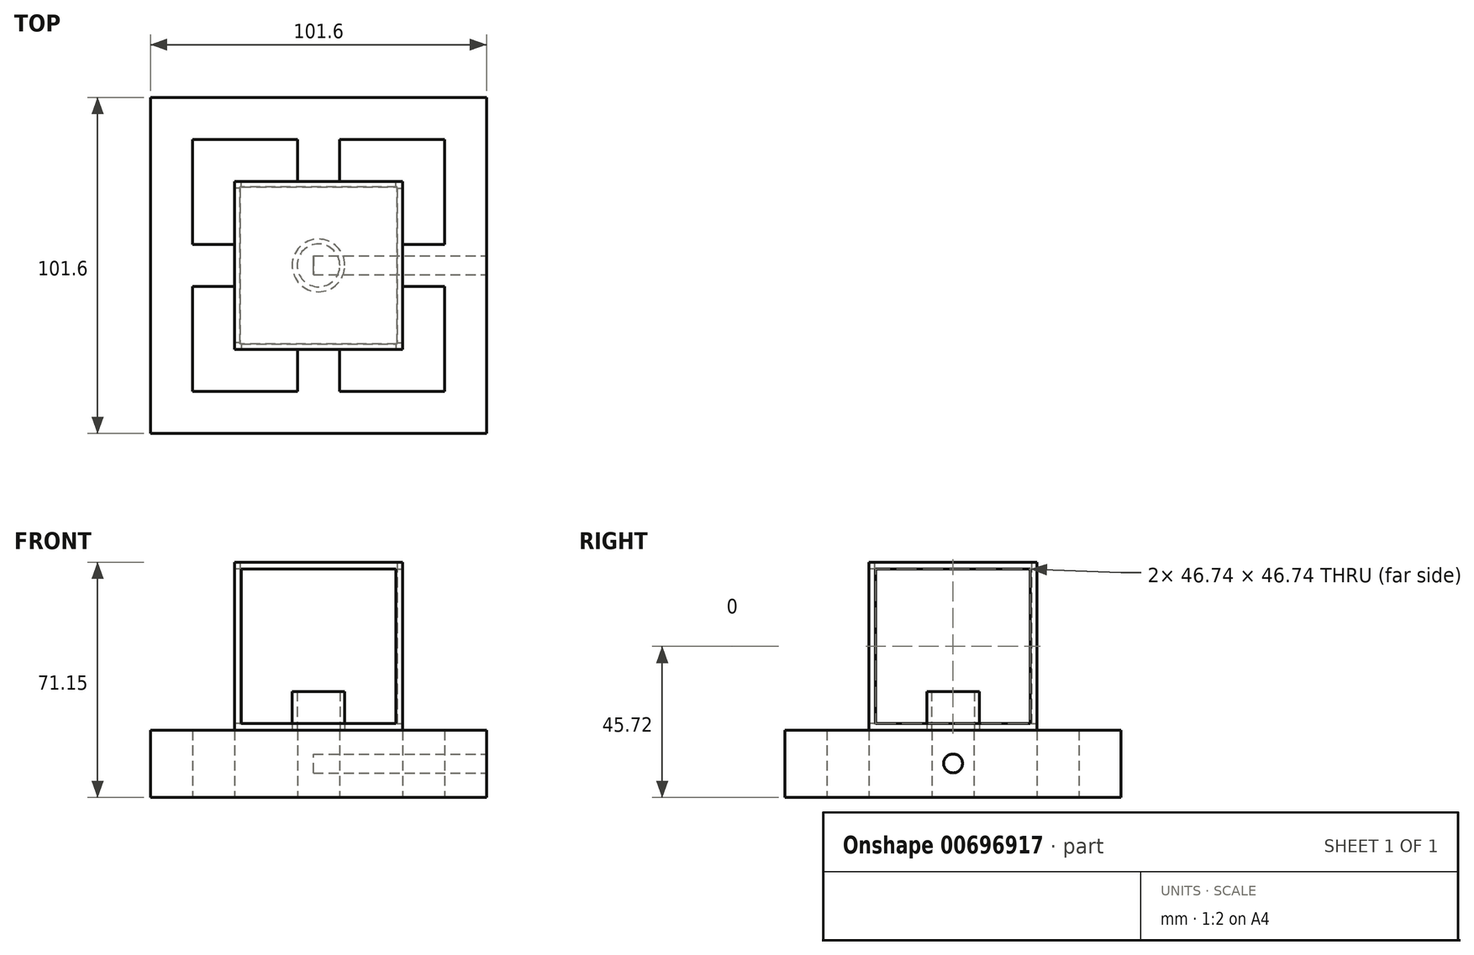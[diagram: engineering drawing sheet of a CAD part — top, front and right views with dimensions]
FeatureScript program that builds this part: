
annotation { "Feature Type Name" : "Feature", "Feature Type Description" : "" }
export const myFeature = defineFeature(function(context is Context, id is Id, definition is map)
    precondition{}
    {
        {
            var Q0;
            Q0=qCreatedBy(makeId("Top.planeOp"),FACE);
            var sketch = newSketch(context, id + "F0", { "sketchPlane" : qUnion([Q0])});
            skLineSegment(sketch, "E0.bottom", {"start": v(50.8, -50.8) * mm, "end": v(-50.8, -50.8) * mm});
            skLineSegment(sketch, "E0.top", {"start": v(50.8, 50.8) * mm, "end": v(-50.8, 50.8) * mm});
            skLineSegment(sketch, "E0.left", {"start": v(50.8, -50.8) * mm, "end": v(50.8, 50.8) * mm});
            skLineSegment(sketch, "E0.right", {"start": v(-50.8, -50.8) * mm, "end": v(-50.8, 50.8) * mm});
            skPoint(sketch, "E0.middle", {"position": v(0, 0) * mm});
            skLineSegment(sketch, "E1.bottom", {"start": v(38.1, -38.1) * mm, "end": v(6.35, -38.1) * mm});
            skLineSegment(sketch, "E1.top", {"start": v(38.1, 38.1) * mm, "end": v(6.35, 38.1) * mm});
            skLineSegment(sketch, "E1.left", {"start": v(38.1, -38.1) * mm, "end": v(38.1, -6.35) * mm});
            skLineSegment(sketch, "E1.right", {"start": v(-38.1, -38.1) * mm, "end": v(-38.1, -6.35) * mm});
            skLineSegment(sketch, "E2.bottom", {"start": v(25.4, -25.4) * mm, "end": v(6.35, -25.4) * mm});
            skLineSegment(sketch, "E2.top", {"start": v(25.4, 25.4) * mm, "end": v(6.35, 25.4) * mm});
            skLineSegment(sketch, "E2.left", {"start": v(25.4, -25.4) * mm, "end": v(25.4, -6.35) * mm});
            skLineSegment(sketch, "E2.right", {"start": v(-25.4, -25.4) * mm, "end": v(-25.4, -6.35) * mm});
            skLineSegment(sketch, "E3.bottom", {"start": v(-25.4, -6.35) * mm, "end": v(-38.1, -6.35) * mm});
            skLineSegment(sketch, "E3.top", {"start": v(-25.4, 6.35) * mm, "end": v(-38.1, 6.35) * mm});
            skPoint(sketch, "E3.middle", {"position": v(-31.54, 0) * mm});
            skPoint(sketch, "E4.middle", {"position": v(0, 32.09) * mm});
            skLineSegment(sketch, "E5.bottom", {"start": v(38.1, -6.35) * mm, "end": v(25.4, -6.35) * mm});
            skLineSegment(sketch, "E5.top", {"start": v(38.1, 6.35) * mm, "end": v(25.4, 6.35) * mm});
            skPoint(sketch, "E5.middle", {"position": v(25.4, 0) * mm});
            skPoint(sketch, "E6.middle", {"position": v(0, -32.64) * mm});
            skPoint(sketch, "E6.middle.positionSnap0", {"position": v(0, -25.4) * mm});
            skPoint(sketch, "E6.centerSnap0", {"position": v(0, -25.4) * mm});
            skPoint(sketch, "E5.right.end.orphan", {"position": v(8.99, 6.35) * mm});
            skPoint(sketch, "E5.right.start.orphan", {"position": v(8.61, -6.35) * mm});
            skPoint(sketch, "E7.orphan", {"position": v(-21.8, 6.35) * mm});
            skPoint(sketch, "E8.orphan", {"position": v(-21.8, -6.35) * mm});
            skPoint(sketch, "E9.orphan", {"position": v(-5.68, 22.96) * mm});
            skPoint(sketch, "E10.orphan", {"position": v(6.35, 20.8) * mm});
            skPoint(sketch, "E11.orphan", {"position": v(42.19, 6.35) * mm});
            skPoint(sketch, "E12.orphan", {"position": v(41.81, -6.35) * mm});
            skPoint(sketch, "E13.orphan", {"position": v(-5.68, -43.1) * mm});
            skPoint(sketch, "E14.orphan", {"position": v(6.35, -43.1) * mm});
            skPoint(sketch, "E15.orphan", {"position": v(-6.35, -22.17) * mm});
            skPoint(sketch, "E16.orphan", {"position": v(5.68, -22.17) * mm});
            skPoint(sketch, "E3.right.end.orphan", {"position": v(-41.26, 6.35) * mm});
            skPoint(sketch, "E17.orphan", {"position": v(-41.26, -6.35) * mm});
            skPoint(sketch, "E18.orphan", {"position": v(-6.35, 43.38) * mm});
            skPoint(sketch, "E19.orphan", {"position": v(5.68, 41.21) * mm});
            skLineSegment(sketch, "E20.bottom", {"start": v(-5.68, -43.1) * mm, "end": v(-6.35, -43.1) * mm});
            skLineSegment(sketch, "E20.top", {"start": v(6.35, -22.17) * mm, "end": v(5.68, -22.17) * mm});
            skLineSegment(sketch, "E20.left", {"start": v(6.35, -38.1) * mm, "end": v(6.35, -25.4) * mm});
            skLineSegment(sketch, "E20.right", {"start": v(-6.35, -38.1) * mm, "end": v(-6.35, -25.4) * mm});
            skLineSegment(sketch, "E21.left", {"start": v(6.35, 25.4) * mm, "end": v(6.35, 38.1) * mm});
            skLineSegment(sketch, "E21.right", {"start": v(-6.35, 25.4) * mm, "end": v(-6.35, 38.1) * mm});
            skPoint(sketch, "E22.orphan", {"position": v(6.35, 43) * mm});
            skPoint(sketch, "E21.bottom.end.orphan", {"position": v(-6.35, 21.16) * mm});
            skLineSegment(sketch, "E23.trimOffspring", {"start": v(-38.1, 6.35) * mm, "end": v(-38.1, 38.1) * mm});
            skLineSegment(sketch, "E24.trimOffspring", {"start": v(-25.4, 6.35) * mm, "end": v(-25.4, 25.4) * mm});
            skLineSegment(sketch, "E25.trimOffspring", {"start": v(-6.35, 25.4) * mm, "end": v(-25.4, 25.4) * mm});
            skLineSegment(sketch, "E26.trimOffspring", {"start": v(-6.35, 38.1) * mm, "end": v(-38.1, 38.1) * mm});
            skLineSegment(sketch, "E27.trimOffspring", {"start": v(25.4, 6.35) * mm, "end": v(25.4, 25.4) * mm});
            skLineSegment(sketch, "E28.trimOffspring", {"start": v(38.1, 6.35) * mm, "end": v(38.1, 38.1) * mm});
            skLineSegment(sketch, "E29.trimOffspring", {"start": v(-6.35, -38.1) * mm, "end": v(-38.1, -38.1) * mm});
            skLineSegment(sketch, "E30.trimOffspring", {"start": v(-6.35, -25.4) * mm, "end": v(-25.4, -25.4) * mm});
            skSolve(sketch);
        }
        {
            var Q0;
            Q0=makeQuery(id+"F0.imprint","IMPRINT",FACE,{"disambiguationData":[TD([[makeQuery(id+"F0.imprint","IMPRINT",EDGE,{"derivedFrom":sQuery(id+"F0.wireOp",EDGE,"E0.bottom")}),-1.0]])]});
            extrude(context, id + "F1", {"entities" : qUnion([Q0]), "depth" : 20.32 * mm, "offsetDistance" : 25.4 * mm});
        }
        {
            var Q0;
            Q0=makeQuery(id+"F1.opExtrude","CAP_FACE",FACE,{"disambiguationData":[OSD([sQuery(id+"F0.wireOp",EDGE,"E0.bottom"),sQuery(id+"F0.wireOp",EDGE,"E0.top"),sQuery(id+"F0.wireOp",EDGE,"E0.left"),sQuery(id+"F0.wireOp",EDGE,"E0.right"),sQuery(id+"F0.wireOp",EDGE,"E1.bottom"),sQuery(id+"F0.wireOp",EDGE,"E1.top"),sQuery(id+"F0.wireOp",EDGE,"E1.left"),sQuery(id+"F0.wireOp",EDGE,"E1.right"),sQuery(id+"F0.wireOp",EDGE,"E2.bottom"),sQuery(id+"F0.wireOp",EDGE,"E2.top"),sQuery(id+"F0.wireOp",EDGE,"E2.left"),sQuery(id+"F0.wireOp",EDGE,"E2.right"),sQuery(id+"F0.wireOp",EDGE,"E3.bottom"),sQuery(id+"F0.wireOp",EDGE,"E3.top"),sQuery(id+"F0.wireOp",EDGE,"E5.bottom"),sQuery(id+"F0.wireOp",EDGE,"E5.top"),sQuery(id+"F0.wireOp",EDGE,"E20.left"),sQuery(id+"F0.wireOp",EDGE,"E20.right"),sQuery(id+"F0.wireOp",EDGE,"E21.left"),sQuery(id+"F0.wireOp",EDGE,"E21.right"),sQuery(id+"F0.wireOp",EDGE,"E23.trimOffspring"),sQuery(id+"F0.wireOp",EDGE,"E24.trimOffspring"),sQuery(id+"F0.wireOp",EDGE,"E25.trimOffspring"),sQuery(id+"F0.wireOp",EDGE,"E26.trimOffspring"),sQuery(id+"F0.wireOp",EDGE,"E27.trimOffspring"),sQuery(id+"F0.wireOp",EDGE,"E28.trimOffspring"),sQuery(id+"F0.wireOp",EDGE,"E29.trimOffspring"),sQuery(id+"F0.wireOp",EDGE,"E30.trimOffspring")])],"isStart":false});
            var sketch = newSketch(context, id + "F2", { "sketchPlane" : qUnion([Q0])});
            skLineSegment(sketch, "E31.bottom", {"start": v(25.4, -25.4) * mm, "end": v(-25.4, -25.4) * mm});
            skLineSegment(sketch, "E31.top", {"start": v(25.4, 25.4) * mm, "end": v(-25.4, 25.4) * mm});
            skLineSegment(sketch, "E31.left", {"start": v(25.4, -25.4) * mm, "end": v(25.4, 25.4) * mm});
            skLineSegment(sketch, "E31.right", {"start": v(-25.4, -25.4) * mm, "end": v(-25.4, 25.4) * mm});
            skPoint(sketch, "E31.middle", {"position": v(0, 0) * mm});
            skLineSegment(sketch, "E32.bottom", {"start": v(23.74, -23.74) * mm, "end": v(-23.74, -23.74) * mm});
            skLineSegment(sketch, "E32.top", {"start": v(23.74, 23.74) * mm, "end": v(-23.74, 23.74) * mm});
            skLineSegment(sketch, "E32.left", {"start": v(23.74, -23.74) * mm, "end": v(23.74, 23.74) * mm});
            skLineSegment(sketch, "E32.right", {"start": v(-23.74, -23.74) * mm, "end": v(-23.74, 23.74) * mm});
            skSolve(sketch);
        }
        {
            var Q0;
            Q0=makeQuery(id+"F2.imprint","IMPRINT",FACE,{"disambiguationData":[TD([[makeQuery(id+"F2.imprint","IMPRINT",EDGE,{"derivedFrom":sQuery(id+"F2.wireOp",EDGE,"E32.bottom")}),1.0]])]});
            extrude(context, id + "F3", {"entities" : qUnion([Q0]), "operationType" : NewBodyOperationType.ADD, "depth" : 50.8 * mm, "offsetDistance" : 25.4 * mm});
        }
        {
            var Q0;
            Q0=makeQuery(id+"F3.boolean.opBoolean","MERGE",FACE,{"derivedFrom":[makeQuery(id+"F1.opExtrude","SWEPT_FACE",FACE,{"disambiguationData":[OSD([sQuery(id+"F0.wireOp",EDGE,"E2.left")])]}),makeQuery(id+"F1.opExtrude","SWEPT_FACE",FACE,{"disambiguationData":[OSD([sQuery(id+"F0.wireOp",EDGE,"E27.trimOffspring")])]}),makeQuery(id+"F3.opExtrude","SWEPT_FACE",FACE,{"disambiguationData":[OSD([sQuery(id+"F2.wireOp",EDGE,"E31.left")])]})]});
            var sketch = newSketch(context, id + "F4", { "sketchPlane" : qUnion([Q0])});
            skLineSegment(sketch, "E33.bottom", {"start": v(-23.37, 69.09) * mm, "end": v(23.37, 69.09) * mm});
            skLineSegment(sketch, "E33.top", {"start": v(-23.37, 22.35) * mm, "end": v(23.37, 22.35) * mm});
            skLineSegment(sketch, "E33.left", {"start": v(-23.37, 69.09) * mm, "end": v(-23.37, 22.35) * mm});
            skLineSegment(sketch, "E33.right", {"start": v(23.37, 69.09) * mm, "end": v(23.37, 22.35) * mm});
            skSolve(sketch);
        }
        {
            var Q0;
            Q0=makeQuery(id+"F4.imprint","IMPRINT",FACE,{"disambiguationData":[TD([[makeQuery(id+"F4.imprint","IMPRINT",EDGE,{"derivedFrom":sQuery(id+"F4.wireOp",EDGE,"E33.bottom")}),-1.0]])]});
            extrude(context, id + "F5", {"entities" : qUnion([Q0]), "operationType" : NewBodyOperationType.REMOVE, "oppositeDirection" : true, "depth" : 25.4 * mm, "offsetDistance" : 25.4 * mm});
        }
        {
            var Q0;
            Q0=makeQuery(id+"F3.boolean.opBoolean","MERGE",FACE,{"derivedFrom":[makeQuery(id+"F1.opExtrude","SWEPT_FACE",FACE,{"disambiguationData":[OSD([sQuery(id+"F0.wireOp",EDGE,"E2.bottom")])]}),makeQuery(id+"F1.opExtrude","SWEPT_FACE",FACE,{"disambiguationData":[OSD([sQuery(id+"F0.wireOp",EDGE,"E30.trimOffspring")])]}),makeQuery(id+"F3.opExtrude","SWEPT_FACE",FACE,{"disambiguationData":[OSD([sQuery(id+"F2.wireOp",EDGE,"E31.bottom")])]})]});
            var sketch = newSketch(context, id + "F6", { "sketchPlane" : qUnion([Q0])});
            skLineSegment(sketch, "E34.bottom", {"start": v(-23.37, 69.09) * mm, "end": v(23.37, 69.09) * mm});
            skLineSegment(sketch, "E34.top", {"start": v(-23.37, 22.35) * mm, "end": v(23.37, 22.35) * mm});
            skLineSegment(sketch, "E34.left", {"start": v(-23.37, 69.09) * mm, "end": v(-23.37, 22.35) * mm});
            skLineSegment(sketch, "E34.right", {"start": v(23.37, 69.09) * mm, "end": v(23.37, 22.35) * mm});
            skSolve(sketch);
        }
        {
            var Q0;
            Q0=makeQuery(id+"F6.imprint","IMPRINT",FACE,{"disambiguationData":[TD([[makeQuery(id+"F6.imprint","IMPRINT",EDGE,{"derivedFrom":sQuery(id+"F6.wireOp",EDGE,"E34.bottom")}),-1.0]])]});
            extrude(context, id + "F7", {"entities" : qUnion([Q0]), "operationType" : NewBodyOperationType.REMOVE, "oppositeDirection" : true, "depth" : 25.4 * mm, "offsetDistance" : 25.4 * mm});
        }
        {
            var Q0;
            Q0=makeQuery(id+"F3.boolean.opBoolean","MERGE",FACE,{"derivedFrom":[makeQuery(id+"F1.opExtrude","SWEPT_FACE",FACE,{"disambiguationData":[OSD([sQuery(id+"F0.wireOp",EDGE,"E2.right")])]}),makeQuery(id+"F1.opExtrude","SWEPT_FACE",FACE,{"disambiguationData":[OSD([sQuery(id+"F0.wireOp",EDGE,"E24.trimOffspring")])]}),makeQuery(id+"F3.opExtrude","SWEPT_FACE",FACE,{"disambiguationData":[OSD([sQuery(id+"F2.wireOp",EDGE,"E31.right")])]})]});
            var sketch = newSketch(context, id + "F8", { "sketchPlane" : qUnion([Q0])});
            skLineSegment(sketch, "E35.bottom", {"start": v(-23.37, 69.09) * mm, "end": v(23.37, 69.09) * mm});
            skLineSegment(sketch, "E35.top", {"start": v(-23.37, 22.35) * mm, "end": v(23.37, 22.35) * mm});
            skLineSegment(sketch, "E35.left", {"start": v(-23.37, 69.09) * mm, "end": v(-23.37, 22.35) * mm});
            skLineSegment(sketch, "E35.right", {"start": v(23.37, 69.09) * mm, "end": v(23.37, 22.35) * mm});
            skSolve(sketch);
        }
        {
            var Q0;
            Q0=makeQuery(id+"F8.imprint","IMPRINT",FACE,{"disambiguationData":[TD([[makeQuery(id+"F8.imprint","IMPRINT",EDGE,{"derivedFrom":sQuery(id+"F8.wireOp",EDGE,"E35.bottom")}),-1.0]])]});
            extrude(context, id + "F9", {"entities" : qUnion([Q0]), "operationType" : NewBodyOperationType.REMOVE, "oppositeDirection" : true, "depth" : 25.4 * mm, "offsetDistance" : 25.4 * mm});
        }
        {
            var Q0;
            Q0=makeQuery(id+"F3.boolean.opBoolean","MERGE",FACE,{"derivedFrom":[makeQuery(id+"F1.opExtrude","SWEPT_FACE",FACE,{"disambiguationData":[OSD([sQuery(id+"F0.wireOp",EDGE,"E2.top")])]}),makeQuery(id+"F1.opExtrude","SWEPT_FACE",FACE,{"disambiguationData":[OSD([sQuery(id+"F0.wireOp",EDGE,"E25.trimOffspring")])]}),makeQuery(id+"F3.opExtrude","SWEPT_FACE",FACE,{"disambiguationData":[OSD([sQuery(id+"F2.wireOp",EDGE,"E31.top")])]})]});
            var sketch = newSketch(context, id + "F10", { "sketchPlane" : qUnion([Q0])});
            skLineSegment(sketch, "E36.bottom", {"start": v(-23.37, 69.09) * mm, "end": v(23.37, 69.09) * mm});
            skLineSegment(sketch, "E36.top", {"start": v(-23.37, 22.35) * mm, "end": v(23.37, 22.35) * mm});
            skLineSegment(sketch, "E36.left", {"start": v(-23.37, 69.09) * mm, "end": v(-23.37, 22.35) * mm});
            skLineSegment(sketch, "E36.right", {"start": v(23.37, 69.09) * mm, "end": v(23.37, 22.35) * mm});
            skSolve(sketch);
        }
        {
            var Q0;
            Q0=makeQuery(id+"F10.imprint","IMPRINT",FACE,{"disambiguationData":[TD([[makeQuery(id+"F10.imprint","IMPRINT",EDGE,{"derivedFrom":sQuery(id+"F10.wireOp",EDGE,"E36.bottom")}),-1.0]])]});
            extrude(context, id + "F11", {"entities" : qUnion([Q0]), "operationType" : NewBodyOperationType.REMOVE, "oppositeDirection" : true, "depth" : 25.4 * mm, "offsetDistance" : 25.4 * mm});
        }
        {
            var Q0;
            Q0=makeQuery(id+"F3.opExtrude","CAP_FACE",FACE,{"disambiguationData":[OSD([sQuery(id+"F2.wireOp",EDGE,"E31.bottom"),sQuery(id+"F2.wireOp",EDGE,"E31.top"),sQuery(id+"F2.wireOp",EDGE,"E31.left"),sQuery(id+"F2.wireOp",EDGE,"E31.right"),sQuery(id+"F2.wireOp",EDGE,"E32.bottom"),sQuery(id+"F2.wireOp",EDGE,"E32.top"),sQuery(id+"F2.wireOp",EDGE,"E32.left"),sQuery(id+"F2.wireOp",EDGE,"E32.right")])],"isStart":false});
            cPlane(context, id + "F12", {"entities" : qUnion([Q0]), "cplaneType" : CPlaneType.OFFSET, "offset" : 0 * mm, "width" : 152.4 * mm, "height" : 152.4 * mm});
        }
        {
            var Q0;
            Q0=qCreatedBy(id+"F12.planeOp",FACE);
            var sketch = newSketch(context, id + "F13", { "sketchPlane" : qUnion([Q0])});
            skLineSegment(sketch, "E37.bottom", {"start": v(-25.4, 25.4) * mm, "end": v(25.4, 25.4) * mm});
            skLineSegment(sketch, "E37.top", {"start": v(-25.4, -25.4) * mm, "end": v(25.4, -25.4) * mm});
            skLineSegment(sketch, "E37.left", {"start": v(-25.4, 25.4) * mm, "end": v(-25.4, -25.4) * mm});
            skLineSegment(sketch, "E37.right", {"start": v(25.4, 25.4) * mm, "end": v(25.4, -25.4) * mm});
            skPoint(sketch, "E37.middle", {"position": v(0, 0) * mm});
            skSolve(sketch);
        }
        {
            var Q0;
            Q0=makeQuery(id+"F13.imprint","IMPRINT",FACE,{"disambiguationData":[TD([[makeQuery(id+"F13.imprint","IMPRINT",EDGE,{"derivedFrom":sQuery(id+"F13.wireOp",EDGE,"E37.bottom")}),-1.0]])]});
            extrude(context, id + "F14", {"entities" : qUnion([Q0]), "operationType" : NewBodyOperationType.ADD, "depth" : 0.03 * mm, "offsetDistance" : 25.4 * mm});
        }
        {
            var Q0;
            Q0=makeQuery(id+"F1.opExtrude","SWEPT_FACE",FACE,{"disambiguationData":[OSD([sQuery(id+"F0.wireOp",EDGE,"E0.left")])]});
            var sketch = newSketch(context, id + "F15", { "sketchPlane" : qUnion([Q0])});
            skCircle(sketch, "E38", {"center": v(0, 10.3) * mm, "radius": 2.86 * mm});
            skPoint(sketch, "E38.centerSnap0", {"position": v(0, 0) * mm});
            skSolve(sketch);
        }
        {
            var Q0;
            Q0=makeQuery(id+"F15.imprint","IMPRINT",FACE,{"disambiguationData":[TD([[makeQuery(id+"F15.imprint","IMPRINT",EDGE,{"derivedFrom":sQuery(id+"F15.wireOp",EDGE,"E38")}),1.0]])]});
            extrude(context, id + "F16", {"entities" : qUnion([Q0]), "operationType" : NewBodyOperationType.REMOVE, "oppositeDirection" : true, "depth" : 52.32 * mm, "offsetDistance" : 25.4 * mm});
        }
        {
            var Q0;
            Q0=makeQuery(id+"F3.boolean.opBoolean","SPLIT",FACE,{"disambiguationData":[TD([makeQuery(id+"F3.opExtrude","SWEPT_FACE",FACE,{"disambiguationData":[OSD([sQuery(id+"F2.wireOp",EDGE,"E32.bottom")])]})])],"derivedFrom":makeQuery(id+"F1.opExtrude","CAP_FACE",FACE,{"disambiguationData":[OSD([sQuery(id+"F0.wireOp",EDGE,"E0.bottom"),sQuery(id+"F0.wireOp",EDGE,"E0.top"),sQuery(id+"F0.wireOp",EDGE,"E0.left"),sQuery(id+"F0.wireOp",EDGE,"E0.right"),sQuery(id+"F0.wireOp",EDGE,"E1.bottom"),sQuery(id+"F0.wireOp",EDGE,"E1.top"),sQuery(id+"F0.wireOp",EDGE,"E1.left"),sQuery(id+"F0.wireOp",EDGE,"E1.right"),sQuery(id+"F0.wireOp",EDGE,"E2.bottom"),sQuery(id+"F0.wireOp",EDGE,"E2.top"),sQuery(id+"F0.wireOp",EDGE,"E2.left"),sQuery(id+"F0.wireOp",EDGE,"E2.right"),sQuery(id+"F0.wireOp",EDGE,"E3.bottom"),sQuery(id+"F0.wireOp",EDGE,"E3.top"),sQuery(id+"F0.wireOp",EDGE,"E5.bottom"),sQuery(id+"F0.wireOp",EDGE,"E5.top"),sQuery(id+"F0.wireOp",EDGE,"E20.left"),sQuery(id+"F0.wireOp",EDGE,"E20.right"),sQuery(id+"F0.wireOp",EDGE,"E21.left"),sQuery(id+"F0.wireOp",EDGE,"E21.right"),sQuery(id+"F0.wireOp",EDGE,"E23.trimOffspring"),sQuery(id+"F0.wireOp",EDGE,"E24.trimOffspring"),sQuery(id+"F0.wireOp",EDGE,"E25.trimOffspring"),sQuery(id+"F0.wireOp",EDGE,"E26.trimOffspring"),sQuery(id+"F0.wireOp",EDGE,"E27.trimOffspring"),sQuery(id+"F0.wireOp",EDGE,"E28.trimOffspring"),sQuery(id+"F0.wireOp",EDGE,"E29.trimOffspring"),sQuery(id+"F0.wireOp",EDGE,"E30.trimOffspring")])],"isStart":false})});
            var sketch = newSketch(context, id + "F17", { "sketchPlane" : qUnion([Q0])});
            skCircle(sketch, "E39", {"center": v(0, 0) * mm, "radius": 6.47 * mm});
            skCircle(sketch, "E40", {"center": v(0, 0) * mm, "radius": 7.96 * mm});
            skSolve(sketch);
        }
        {
            var Q0;
            Q0=makeQuery(id+"F17.imprint","IMPRINT",FACE,{"disambiguationData":[TD([[makeQuery(id+"F17.imprint","IMPRINT",EDGE,{"derivedFrom":sQuery(id+"F17.wireOp",EDGE,"E39")}),-1.0]])]});
            extrude(context, id + "F18", {"entities" : qUnion([Q0]), "operationType" : NewBodyOperationType.ADD, "depth" : 11.73 * mm, "offsetDistance" : 25.4 * mm});
        }
    });
